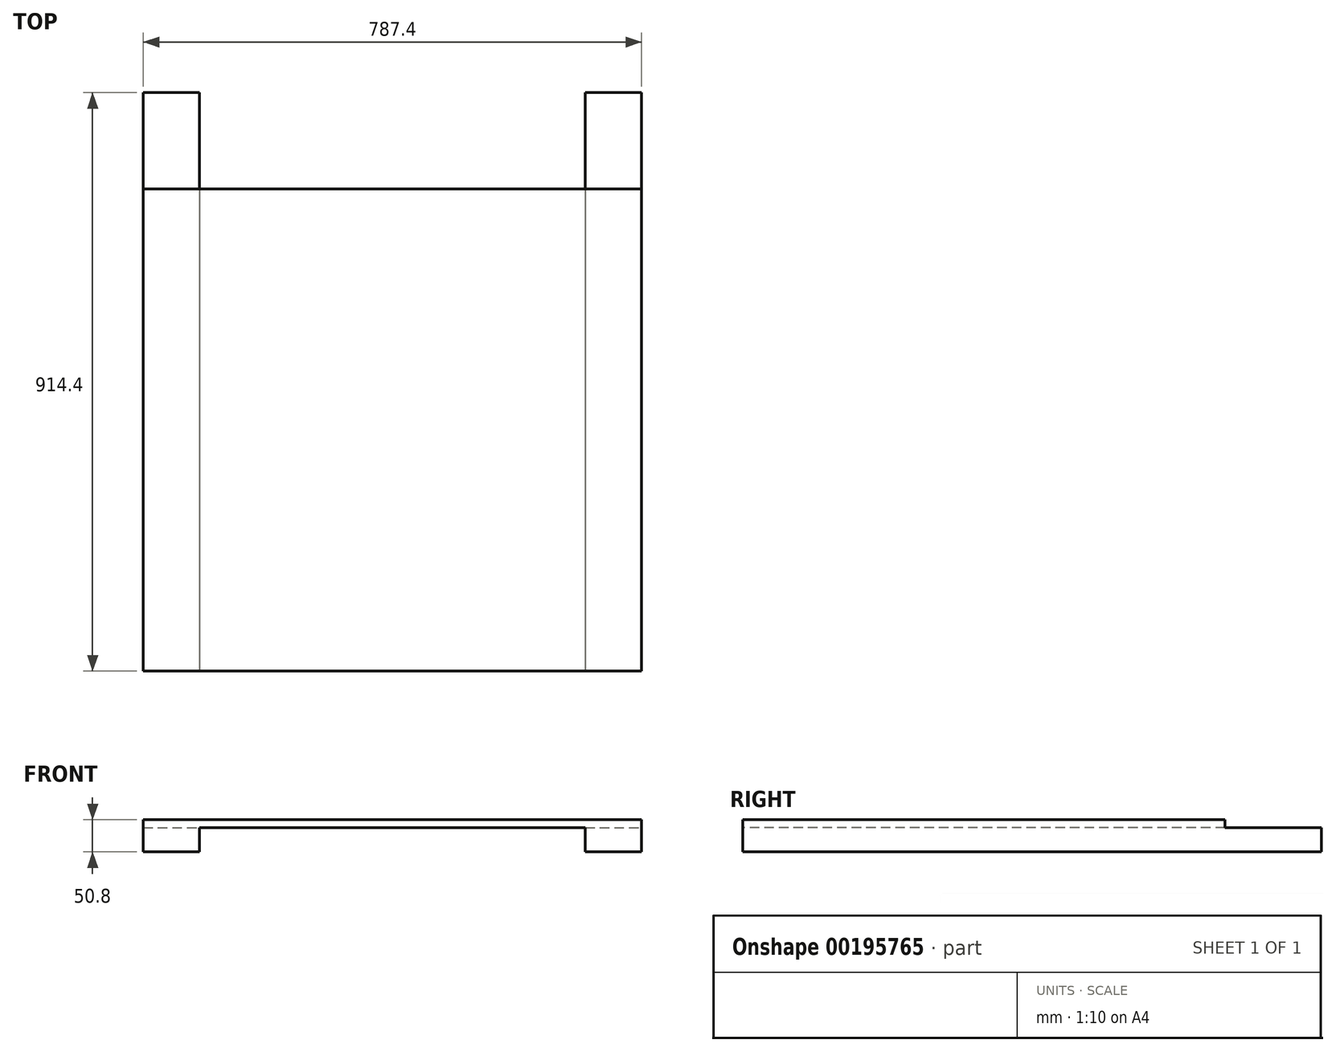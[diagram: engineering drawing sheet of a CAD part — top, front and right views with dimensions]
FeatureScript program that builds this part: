
annotation { "Feature Type Name" : "Feature", "Feature Type Description" : "" }
export const myFeature = defineFeature(function(context is Context, id is Id, definition is map)
    precondition{}
    {
        {
            var Q0;
            Q0=qCreatedBy(makeId("Front.planeOp"),FACE);
            var sketch = newSketch(context, id + "F0", { "sketchPlane" : qUnion([Q0])});
            skLineSegment(sketch, "E0.bottom", {"start": v(0, 0) * mm, "end": v(787.4, 0) * mm});
            skLineSegment(sketch, "E0.top", {"start": v(0, 12.7) * mm, "end": v(787.4, 12.7) * mm});
            skLineSegment(sketch, "E0.left", {"start": v(0, 0) * mm, "end": v(0, 12.7) * mm});
            skLineSegment(sketch, "E0.right", {"start": v(787.4, 0) * mm, "end": v(787.4, 12.7) * mm});
            skSolve(sketch);
        }
        {
            var Q0;
            Q0=makeQuery(id+"F0.imprint","IMPRINT",FACE,{"disambiguationData":[TD([[makeQuery(id+"F0.imprint","IMPRINT",EDGE,{"derivedFrom":sQuery(id+"F0.wireOp",EDGE,"E0.bottom")}),1.0]])]});
            extrude(context, id + "F1", {"entities" : qUnion([Q0]), "depth" : 762 * mm});
        }
        {
            var Q0;
            Q0=makeQuery(id+"F1.opExtrude","CAP_FACE",FACE,{"disambiguationData":[OSD([sQuery(id+"F0.wireOp",EDGE,"E0.bottom"),sQuery(id+"F0.wireOp",EDGE,"E0.top"),sQuery(id+"F0.wireOp",EDGE,"E0.left"),sQuery(id+"F0.wireOp",EDGE,"E0.right")])],"isStart":false});
            var sketch = newSketch(context, id + "F2", { "sketchPlane" : qUnion([Q0])});
            skLineSegment(sketch, "E1", {"start": v(393.7, 12.7) * mm, "end": v(393.7, 0) * mm, "construction": true});
            skLineSegment(sketch, "E2.bottom", {"start": v(0, 0) * mm, "end": v(88.9, 0) * mm});
            skLineSegment(sketch, "E2.top", {"start": v(0, -38.1) * mm, "end": v(88.9, -38.1) * mm});
            skLineSegment(sketch, "E2.left", {"start": v(0, 0) * mm, "end": v(0, -38.1) * mm});
            skLineSegment(sketch, "E2.right", {"start": v(88.9, 0) * mm, "end": v(88.9, -38.1) * mm});
            skLineSegment(sketch, "E3.MirrorCS", {"start": v(698.5, 0) * mm, "end": v(698.5, -38.1) * mm});
            skLineSegment(sketch, "E4.MirrorCS", {"start": v(787.4, 0) * mm, "end": v(698.5, 0) * mm});
            skLineSegment(sketch, "E5.MirrorCS", {"start": v(787.4, 0) * mm, "end": v(787.4, -38.1) * mm});
            skLineSegment(sketch, "E6.MirrorCS", {"start": v(787.4, -38.1) * mm, "end": v(698.5, -38.1) * mm});
            skSolve(sketch);
        }
        {
            var Q0;
            Q0=makeQuery(id+"F2.imprint","IMPRINT",FACE,{"disambiguationData":[TD([[makeQuery(id+"F2.imprint","IMPRINT",EDGE,{"derivedFrom":sQuery(id+"F2.wireOp",EDGE,"E2.bottom")}),-1.0]])]});
            var Q1;
            Q1=makeQuery(id+"F2.imprint","IMPRINT",FACE,{"disambiguationData":[TD([[makeQuery(id+"F2.imprint","IMPRINT",EDGE,{"derivedFrom":sQuery(id+"F2.wireOp",EDGE,"E3.MirrorCS")}),1.0]])]});
            extrude(context, id + "F3", {"entities" : qUnion([Q0, Q1]), "operationType" : NewBodyOperationType.ADD, "oppositeDirection" : true, "depth" : 914.4 * mm});
        }
    });
